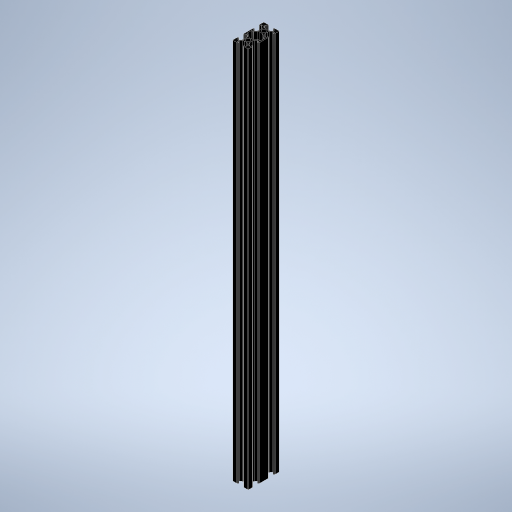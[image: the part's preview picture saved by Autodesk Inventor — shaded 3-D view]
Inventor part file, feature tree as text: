
AUTODESK INVENTOR PART (.ipt)
format: ipt  version: 2023 (Build 270158000, 158)  size: 489,472 bytes
history: native  units: mm
features: other x1, extrude x1, sketch x1
ambient origin geometry x8: Origin, YZ Plane, XZ Plane, XY Plane, X Axis, Y Axis, Z Axis, Center Point
bodies: Body1 (feature_tree)
feature tree (3):
  other  "Sólido1"
  extrude  "Extrusão1"  TaperAngle=45.0deg  [1 undecoded]
  sketch  "Esboço2"  dims[d137=4.5mm d138=45.0deg d139=6.4mm d141=1.5mm d142=1.5mm d145=0.4mm d146=6.5mm d147=45.0deg d148=1.0mm d151=20.0mm d152=20.0mm d153=5.2mm d154=7.4mm d155=13.6mm d156=3.0mm d157=135.0deg d158=3.0mm d159=5.0mm d160=5.0mm d161=0.4mm d162=490.0mm d163=0.0mm]
note: 1 required parameter value undecoded (feature->parameter linkage not recoverable at this tier; creation-order binding heuristic only, values carry confidence <= 0.55)
